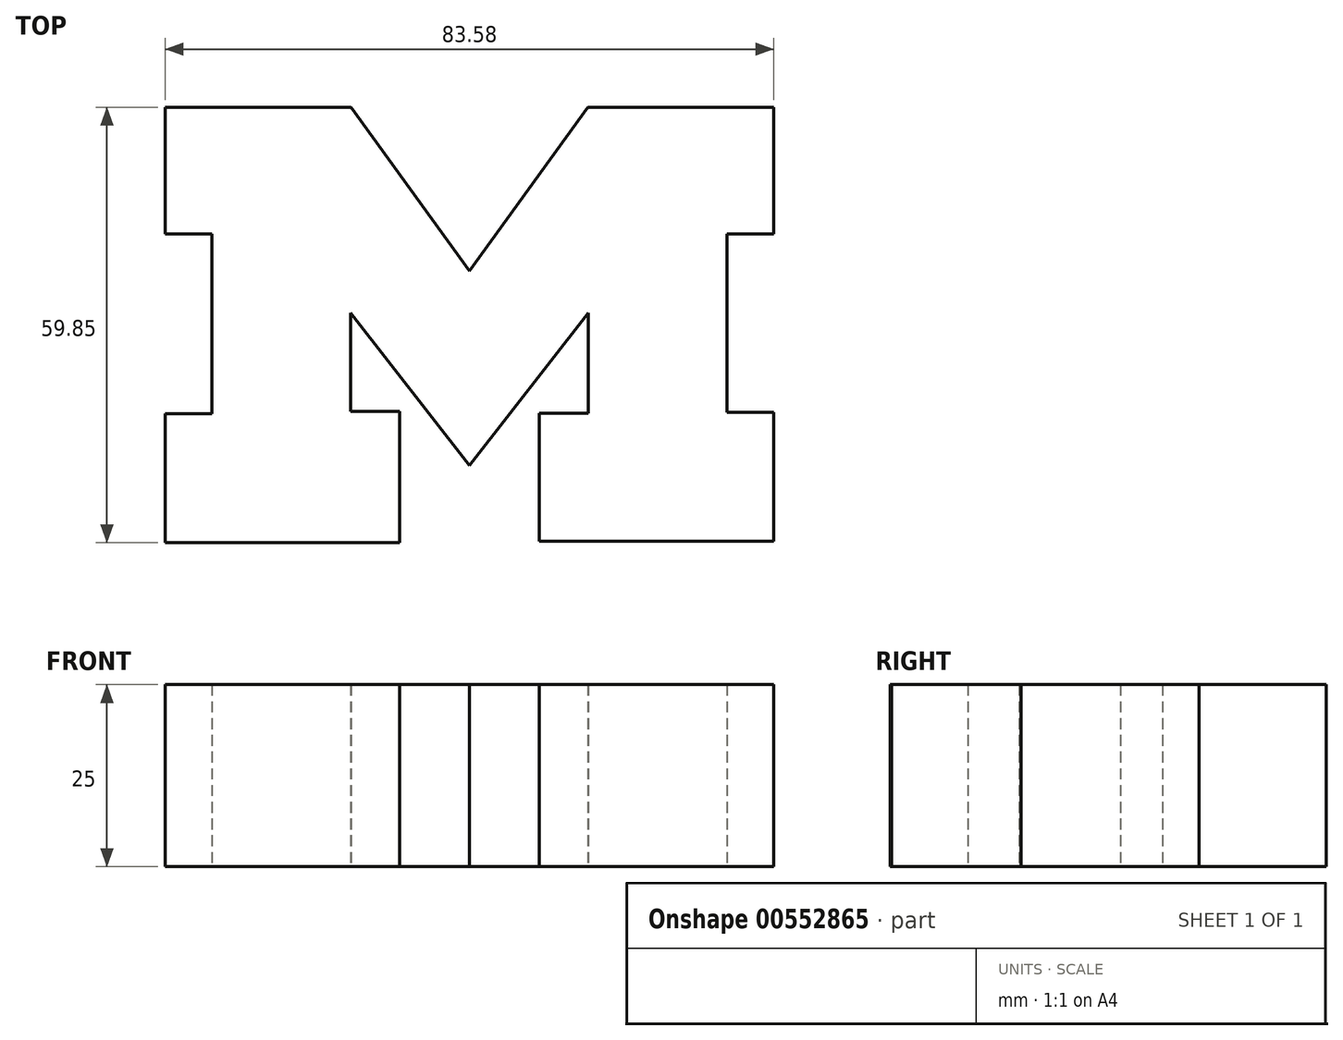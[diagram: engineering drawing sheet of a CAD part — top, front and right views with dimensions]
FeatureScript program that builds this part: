
annotation { "Feature Type Name" : "Feature", "Feature Type Description" : "" }
export const myFeature = defineFeature(function(context is Context, id is Id, definition is map)
    precondition{}
    {
        {
            var Q0;
            Q0=qCreatedBy(makeId("Top.planeOp"),FACE);
            var sketch = newSketch(context, id + "F0", { "sketchPlane" : qUnion([Q0])});
            skLineSegment(sketch, "E0", {"start": v(-41.8, 25.75) * mm, "end": v(-16.23, 25.75) * mm});
            skLineSegment(sketch, "E1", {"start": v(-16.23, 25.75) * mm, "end": v(0, 3.3) * mm});
            skLineSegment(sketch, "E2", {"start": v(0, 3.3) * mm, "end": v(16.23, 25.75) * mm});
            skLineSegment(sketch, "E3", {"start": v(16.23, 25.75) * mm, "end": v(41.8, 25.75) * mm});
            skLineSegment(sketch, "E4", {"start": v(41.8, 25.75) * mm, "end": v(41.8, 8.34) * mm});
            skLineSegment(sketch, "E5", {"start": v(41.8, 8.34) * mm, "end": v(35.35, 8.34) * mm});
            skLineSegment(sketch, "E6", {"start": v(35.35, 8.34) * mm, "end": v(35.35, -16.16) * mm});
            skLineSegment(sketch, "E7", {"start": v(35.35, -16.16) * mm, "end": v(41.8, -16.16) * mm});
            skLineSegment(sketch, "E8", {"start": v(41.8, -16.16) * mm, "end": v(41.8, -33.89) * mm});
            skLineSegment(sketch, "E9", {"start": v(41.8, -33.89) * mm, "end": v(9.57, -33.89) * mm});
            skLineSegment(sketch, "E10", {"start": v(9.57, -33.89) * mm, "end": v(9.57, -16.26) * mm});
            skLineSegment(sketch, "E11", {"start": v(9.57, -16.26) * mm, "end": v(16.34, -16.26) * mm});
            skLineSegment(sketch, "E12", {"start": v(16.34, -16.26) * mm, "end": v(16.34, -2.5) * mm});
            skLineSegment(sketch, "E13", {"start": v(16.34, -2.5) * mm, "end": v(0, -23.46) * mm});
            skLineSegment(sketch, "E14", {"start": v(0, -23.46) * mm, "end": v(-16.34, -2.5) * mm});
            skLineSegment(sketch, "E15", {"start": v(-16.34, -2.5) * mm, "end": v(-16.34, -16.05) * mm});
            skLineSegment(sketch, "E16", {"start": v(-16.34, -16.05) * mm, "end": v(-9.57, -16.05) * mm});
            skLineSegment(sketch, "E17", {"start": v(-9.57, -16.05) * mm, "end": v(-9.57, -34.1) * mm});
            skLineSegment(sketch, "E18", {"start": v(-9.57, -34.1) * mm, "end": v(-41.8, -34.1) * mm});
            skLineSegment(sketch, "E19", {"start": v(-41.8, -34.1) * mm, "end": v(-41.8, -16.37) * mm});
            skLineSegment(sketch, "E20", {"start": v(-41.8, -16.37) * mm, "end": v(-35.35, -16.37) * mm});
            skLineSegment(sketch, "E21", {"start": v(-35.35, -16.37) * mm, "end": v(-35.35, 8.34) * mm});
            skLineSegment(sketch, "E22", {"start": v(-35.35, 8.34) * mm, "end": v(-41.8, 8.34) * mm});
            skLineSegment(sketch, "E23", {"start": v(-41.8, 8.34) * mm, "end": v(-41.8, 25.75) * mm});
            skSolve(sketch);
        }
        {
            var Q0;
            Q0=makeQuery(id+"F0.imprint","IMPRINT",FACE,{"disambiguationData":[TD([[makeQuery(id+"F0.imprint","IMPRINT",EDGE,{"derivedFrom":sQuery(id+"F0.wireOp",EDGE,"E0")}),-1.0]])]});
            extrude(context, id + "F1", {"entities" : qUnion([Q0]), "depth" : 25 * mm, "offsetDistance" : 25 * mm});
        }
    });
